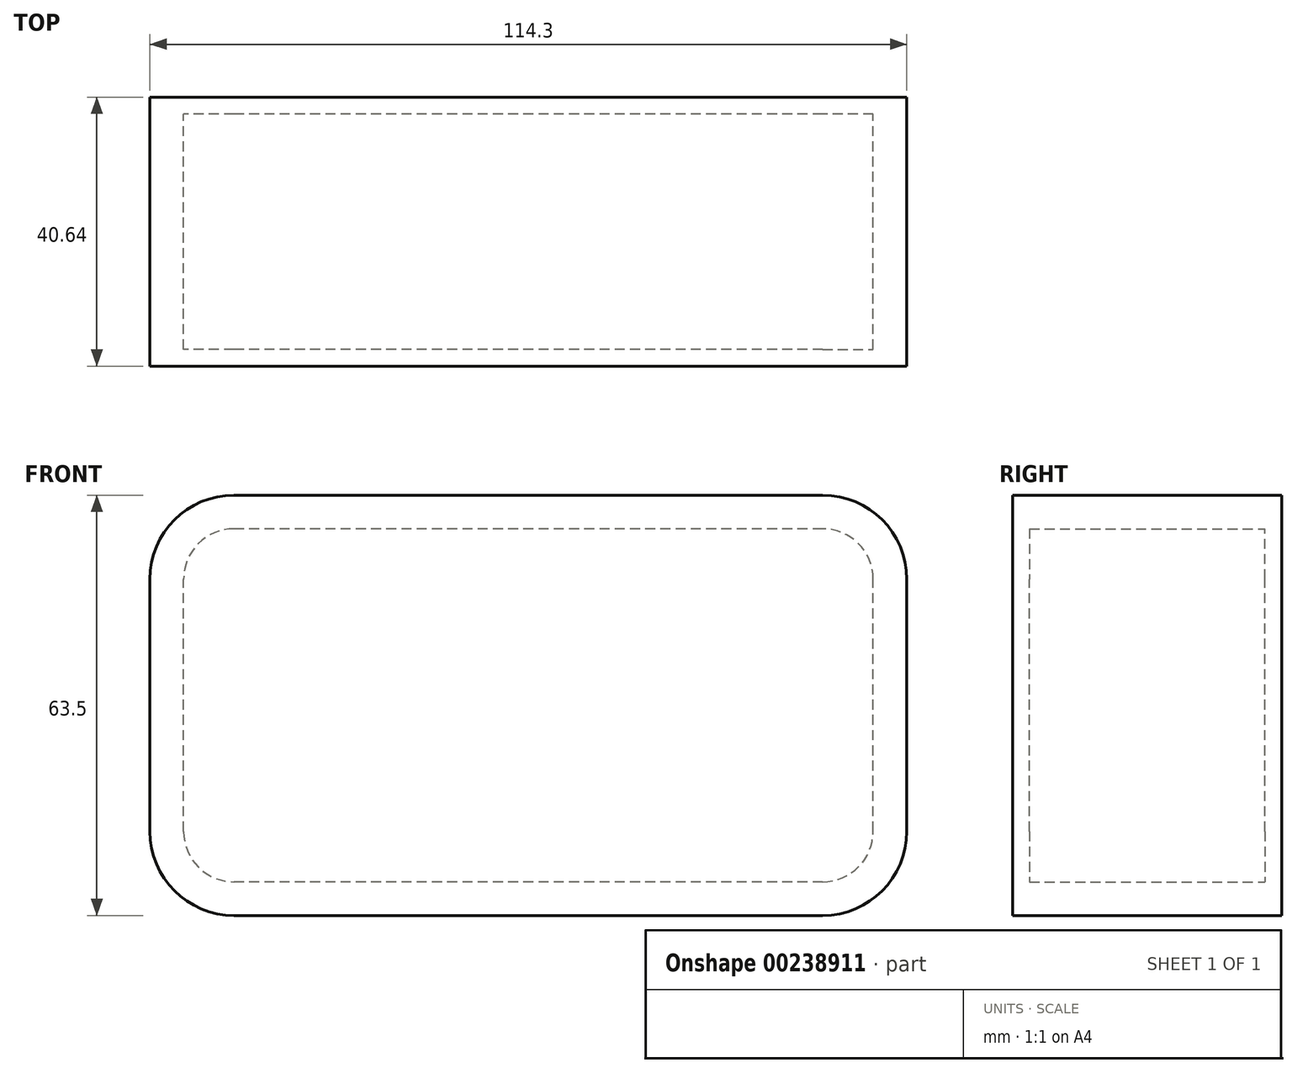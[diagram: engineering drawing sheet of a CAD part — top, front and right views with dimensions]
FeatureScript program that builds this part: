
annotation { "Feature Type Name" : "Feature", "Feature Type Description" : "" }
export const myFeature = defineFeature(function(context is Context, id is Id, definition is map)
    precondition{}
    {
        {
            var Q0;
            Q0=qCreatedBy(makeId("Front.planeOp"),FACE);
            var sketch = newSketch(context, id + "F5", { "sketchPlane" : qUnion([Q0])});
            skLineSegment(sketch, "E0.bottom", {"start": v(57.15, -31.75) * mm, "end": v(-57.15, -31.75) * mm});
            skLineSegment(sketch, "E0.top", {"start": v(57.15, 31.75) * mm, "end": v(-57.15, 31.75) * mm});
            skLineSegment(sketch, "E0.left", {"start": v(57.15, -31.75) * mm, "end": v(57.15, 31.75) * mm});
            skLineSegment(sketch, "E0.right", {"start": v(-57.15, -31.75) * mm, "end": v(-57.15, 31.75) * mm});
            skPoint(sketch, "E0.middle", {"position": v(0, 0) * mm});
            skSolve(sketch);
        }
        {
            var Q0;
            Q0=makeQuery(id+"F5.imprint","IMPRINT",FACE,{"disambiguationData":[TD([[makeQuery(id+"F5.imprint","IMPRINT",EDGE,{"derivedFrom":sQuery(id+"F5.wireOp",EDGE,"E0.bottom")}),-1.0]])]});
            extrude(context, id + "F6", {"entities" : qUnion([Q0]), "depth" : 38.1 * mm});
        }
        {
            var Q0;
            Q0=makeQuery(id+"F6.opExtrude","SWEPT_EDGE",EDGE,{"disambiguationData":[OSD([sQuery(id+"F5.wireOp",EDGE,"E0.top"),sQuery(id+"F5.wireOp",EDGE,"E0.left")])]});
            var Q1;
            Q1=makeQuery(id+"F6.opExtrude","SWEPT_EDGE",EDGE,{"disambiguationData":[OSD([sQuery(id+"F5.wireOp",EDGE,"E0.bottom"),sQuery(id+"F5.wireOp",EDGE,"E0.left")])]});
            var Q2;
            Q2=makeQuery(id+"F6.opExtrude","SWEPT_EDGE",EDGE,{"disambiguationData":[OSD([sQuery(id+"F5.wireOp",EDGE,"E0.bottom"),sQuery(id+"F5.wireOp",EDGE,"E0.right")])]});
            var Q3;
            Q3=makeQuery(id+"F6.opExtrude","SWEPT_EDGE",EDGE,{"disambiguationData":[OSD([sQuery(id+"F5.wireOp",EDGE,"E0.top"),sQuery(id+"F5.wireOp",EDGE,"E0.right")])]});
            fillet(context, id + "F0", {"entities" : qUnion([Q0, Q1, Q2, Q3]), "radius" : 12.7 * mm, "tangentPropagation" : true, "allowEdgeOverflow" : false});
        }
        {
            var Q0;
            Q0=makeQuery(id+"F6.opExtrude","CAP_FACE",FACE,{"disambiguationData":[OSD([sQuery(id+"F5.wireOp",EDGE,"E0.bottom"),sQuery(id+"F5.wireOp",EDGE,"E0.top"),sQuery(id+"F5.wireOp",EDGE,"E0.left"),sQuery(id+"F5.wireOp",EDGE,"E0.right")])],"isStart":false});
            shell(context, id + "F1", {"entities" : qUnion([Q0]), "thickness" : 2.54 * mm});
        }
        {
            var Q0;
            Q0=makeQuery(id+"F1.opShell","OFFSET_FACE",FACE,{"disambiguationData":[OSD([sQuery(id+"F5.wireOp",EDGE,"E0.bottom"),sQuery(id+"F5.wireOp",EDGE,"E0.top"),sQuery(id+"F5.wireOp",EDGE,"E0.left"),sQuery(id+"F5.wireOp",EDGE,"E0.right")])]});
            var sketch = newSketch(context, id + "F7", { "sketchPlane" : qUnion([Q0])});
            skLineSegment(sketch, "E1.0", {"start": v(44.45, 29.21) * mm, "end": v(-44.45, 29.21) * mm});
            skArc(sketch, "E2.0", {"start": v(44.45, 29.21) * mm, "mid": v(51.63, 26.23) * mm, "end": v(54.6, 19.05) * mm});
            skLineSegment(sketch, "E3.0", {"start": v(54.61, -19.05) * mm, "end": v(54.61, 19.05) * mm});
            skArc(sketch, "E4.0", {"start": v(54.61, -19.05) * mm, "mid": v(51.63, -26.23) * mm, "end": v(44.45, -29.2) * mm});
            skLineSegment(sketch, "E5.0", {"start": v(44.45, -29.2) * mm, "end": v(-44.45, -29.21) * mm});
            skArc(sketch, "E6.0", {"start": v(-44.45, -29.21) * mm, "mid": v(-51.63, -26.23) * mm, "end": v(-54.6, -19.05) * mm});
            skLineSegment(sketch, "E7.0", {"start": v(-54.61, -19.05) * mm, "end": v(-54.61, 19.05) * mm});
            skArc(sketch, "E8.0", {"start": v(-54.61, 19.05) * mm, "mid": v(-51.63, 26.23) * mm, "end": v(-44.45, 29.21) * mm});
            skArc(sketch, "E9.0", {"start": v(44.45, 26.67) * mm, "mid": v(49.84, 24.44) * mm, "end": v(52.07, 19.05) * mm});
            skLineSegment(sketch, "E9.1", {"start": v(52.07, -19.05) * mm, "end": v(52.07, 19.05) * mm});
            skLineSegment(sketch, "E9.2", {"start": v(44.45, 26.67) * mm, "end": v(-44.45, 26.67) * mm});
            skArc(sketch, "E9.3", {"start": v(52.07, -19.05) * mm, "mid": v(49.84, -24.44) * mm, "end": v(44.45, -26.67) * mm});
            skArc(sketch, "E9.4", {"start": v(-52.07, 19.05) * mm, "mid": v(-49.84, 24.44) * mm, "end": v(-44.45, 26.67) * mm});
            skLineSegment(sketch, "E9.5", {"start": v(-52.07, -19.05) * mm, "end": v(-52.07, 19.05) * mm});
            skArc(sketch, "E9.6", {"start": v(-44.45, -26.67) * mm, "mid": v(-49.84, -24.44) * mm, "end": v(-52.07, -19.05) * mm});
            skLineSegment(sketch, "E9.7", {"start": v(44.45, -26.67) * mm, "end": v(-44.45, -26.67) * mm});
            skSolve(sketch);
        }
        {
            var Q0;
            Q0=makeQuery(id+"F7.imprint","IMPRINT",FACE,{"disambiguationData":[TD([[makeQuery(id+"F7.imprint","IMPRINT",EDGE,{"derivedFrom":sQuery(id+"F7.wireOp",EDGE,"E1.0")}),1.0]])]});
            extrude(context, id + "F8", {"entities" : qUnion([Q0]), "operationType" : NewBodyOperationType.ADD, "depth" : 7.62 * mm});
        }
        {
            var Q0;
            Q0=makeQuery(id+"F8.opExtrude","CAP_FACE",FACE,{"disambiguationData":[OSD([sQuery(id+"F7.wireOp",EDGE,"E1.0"),sQuery(id+"F7.wireOp",EDGE,"E2.0"),sQuery(id+"F7.wireOp",EDGE,"E3.0"),sQuery(id+"F7.wireOp",EDGE,"E4.0"),sQuery(id+"F7.wireOp",EDGE,"E5.0"),sQuery(id+"F7.wireOp",EDGE,"E6.0"),sQuery(id+"F7.wireOp",EDGE,"E7.0"),sQuery(id+"F7.wireOp",EDGE,"E8.0"),sQuery(id+"F7.wireOp",EDGE,"E9.0"),sQuery(id+"F7.wireOp",EDGE,"E9.1"),sQuery(id+"F7.wireOp",EDGE,"E9.2"),sQuery(id+"F7.wireOp",EDGE,"E9.3"),sQuery(id+"F7.wireOp",EDGE,"E9.4"),sQuery(id+"F7.wireOp",EDGE,"E9.5"),sQuery(id+"F7.wireOp",EDGE,"E9.6"),sQuery(id+"F7.wireOp",EDGE,"E9.7")])],"isStart":false});
            extrude(context, id + "F9", {"entities" : qUnion([Q0]), "depth" : 27.94 * mm});
        }
        {
            var Q0;
            Q0=makeQuery(id+"F6.opExtrude","CAP_FACE",FACE,{"disambiguationData":[OSD([sQuery(id+"F5.wireOp",EDGE,"E0.bottom"),sQuery(id+"F5.wireOp",EDGE,"E0.top"),sQuery(id+"F5.wireOp",EDGE,"E0.left"),sQuery(id+"F5.wireOp",EDGE,"E0.right")])],"isStart":false});
            var sketch = newSketch(context, id + "F2", { "sketchPlane" : qUnion([Q0])});
            skLineSegment(sketch, "E10.0", {"start": v(57.15, -19.05) * mm, "end": v(57.15, 19.05) * mm});
            skArc(sketch, "E11.1", {"start": v(44.45, -31.75) * mm, "mid": v(53.43, -28.03) * mm, "end": v(57.15, -19.05) * mm});
            skPoint(sketch, "E12.0", {"position": v(44.45, -31.75) * mm});
            skLineSegment(sketch, "E13.0", {"start": v(44.45, -31.75) * mm, "end": v(-44.45, -31.75) * mm});
            skArc(sketch, "E14.0", {"start": v(-57.15, -19.05) * mm, "mid": v(-53.43, -28.03) * mm, "end": v(-44.45, -31.75) * mm});
            skLineSegment(sketch, "E15.0", {"start": v(-57.15, -19.05) * mm, "end": v(-57.15, 19.05) * mm});
            skArc(sketch, "E16.0", {"start": v(-44.45, 31.75) * mm, "mid": v(-53.43, 28.03) * mm, "end": v(-57.15, 19.05) * mm});
            skLineSegment(sketch, "E17.0", {"start": v(44.45, 31.75) * mm, "end": v(-44.45, 31.75) * mm});
            skArc(sketch, "E18.0", {"start": v(57.15, 19.05) * mm, "mid": v(53.43, 28.03) * mm, "end": v(44.45, 31.75) * mm});
            skSolve(sketch);
        }
        {
            var Q0;
            Q0 = qSketchRegion(id + "F2", true);
            extrude(context, id + "F3", {"entities" : qUnion([Q0]), "operationType" : NewBodyOperationType.ADD, "depth" : 2.54 * mm});
        }
    });
